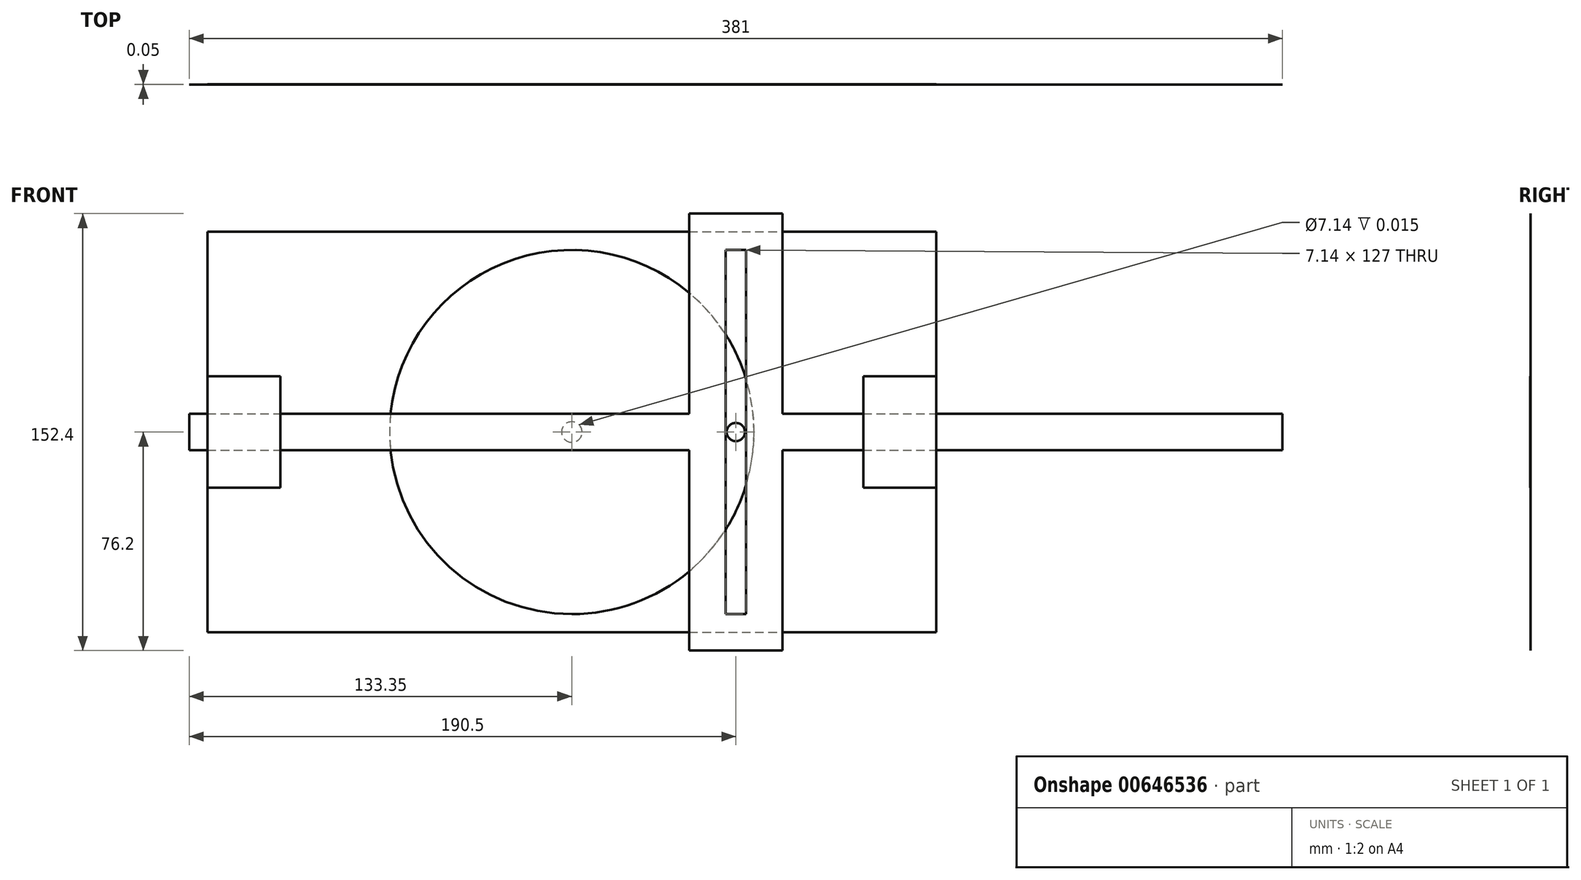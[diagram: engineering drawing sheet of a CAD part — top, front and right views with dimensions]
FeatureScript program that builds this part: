
annotation { "Feature Type Name" : "Feature", "Feature Type Description" : "" }
export const myFeature = defineFeature(function(context is Context, id is Id, definition is map)
    precondition{}
    {
        {
            assignVariable(context, id + "F0", {"name" : "tol", "anyValue" : 1 / 1625.6 * mm});
        }
        {
            assignVariable(context, id + "F1", {"name" : "mat", "anyValue" : 3 / 203.2 * mm});
        }
        {
            var Q0;
            Q0=qCreatedBy(makeId("Front.planeOp"),FACE);
            var sketch = newSketch(context, id + "F2", { "sketchPlane" : qUnion([Q0])});
            skCircle(sketch, "E0", {"center": v(0, 0) * mm, "radius": 63.5 * mm});
            skCircle(sketch, "E1", {"center": v(0, 0) * mm, "radius": 3.18 * mm});
            skCircle(sketch, "E2.0", {"center": v(0, 0) * mm, "radius": 3.57 * mm});
            skSolve(sketch);
        }
        {
            var Q0;
            Q0=makeQuery(id+"F2.imprint","IMPRINT",FACE,{"disambiguationData":[TD([[makeQuery(id+"F2.imprint","IMPRINT",EDGE,{"derivedFrom":sQuery(id+"F2.wireOp",EDGE,"E0")}),1.0]])]});
            extrude(context, id + "F3", {"entities" : qUnion([Q0]), "depth" : getVariable(context, 'mat'), "offsetDistance" : 25.4 * mm});
        }
        {
            var Q0;
            Q0=makeQuery(id+"F3.opExtrude","CAP_FACE",FACE,{"disambiguationData":[OSD([sQuery(id+"F2.wireOp",EDGE,"E0"),sQuery(id+"F2.wireOp",EDGE,"E2.0")])],"isStart":false});
            var sketch = newSketch(context, id + "F4", { "sketchPlane" : qUnion([Q0])});
            skCircle(sketch, "E3", {"center": v(57.15, 0) * mm, "radius": 3.18 * mm});
            skSolve(sketch);
        }
        {
            var Q0;
            Q0=makeQuery(id+"F4.imprint","IMPRINT",FACE,{"disambiguationData":[TD([[makeQuery(id+"F4.imprint","IMPRINT",EDGE,{"derivedFrom":sQuery(id+"F4.wireOp",EDGE,"E3")}),1.0]])]});
            extrude(context, id + "F5", {"entities" : qUnion([Q0]), "operationType" : NewBodyOperationType.ADD, "depth" : getVariable(context, 'mat') * 2, "offsetDistance" : 25.4 * mm});
        }
        {
            var Q0;
            Q0=makeQuery(id+"F3.opExtrude","CAP_FACE",FACE,{"disambiguationData":[OSD([sQuery(id+"F2.wireOp",EDGE,"E0"),sQuery(id+"F2.wireOp",EDGE,"E2.0")])],"isStart":false});
            var sketch = newSketch(context, id + "F6", { "sketchPlane" : qUnion([Q0])});
            skLineSegment(sketch, "E4.bottom", {"start": v(60.72, 63.5) * mm, "end": v(53.58, 63.5) * mm});
            skLineSegment(sketch, "E4.top", {"start": v(60.72, -63.5) * mm, "end": v(53.58, -63.5) * mm});
            skLineSegment(sketch, "E4.left", {"start": v(60.72, 63.5) * mm, "end": v(60.72, -63.5) * mm});
            skLineSegment(sketch, "E4.right", {"start": v(53.58, 63.5) * mm, "end": v(53.58, -63.5) * mm});
            skPoint(sketch, "E4.middle", {"position": v(57.15, 0) * mm});
            skLineSegment(sketch, "E5.bottom", {"start": v(40.88, 76.2) * mm, "end": v(73.42, 76.2) * mm});
            skLineSegment(sketch, "E5.top", {"start": v(40.88, -76.2) * mm, "end": v(73.42, -76.2) * mm});
            skLineSegment(sketch, "E5.left", {"start": v(40.88, 76.2) * mm, "end": v(40.88, -76.2) * mm});
            skLineSegment(sketch, "E5.right", {"start": v(73.42, 76.2) * mm, "end": v(73.42, -76.2) * mm});
            skLineSegment(sketch, "E6.bottom", {"start": v(-133.35, 6.35) * mm, "end": v(247.65, 6.35) * mm});
            skLineSegment(sketch, "E6.top", {"start": v(-133.35, -6.35) * mm, "end": v(247.65, -6.35) * mm});
            skLineSegment(sketch, "E6.left", {"start": v(-133.35, 6.35) * mm, "end": v(-133.35, -6.35) * mm});
            skLineSegment(sketch, "E6.right", {"start": v(247.65, 6.35) * mm, "end": v(247.65, -6.35) * mm});
            skSolve(sketch);
        }
        {
            var Q0;
            Q0 = qSketchRegion(id + "F6", true);
            extrude(context, id + "F7", {"entities" : qUnion([Q0]), "depth" : getVariable(context, 'mat'), "offsetDistance" : 25.4 * mm});
        }
        {
            var Q0;
            Q0=qCreatedBy(makeId("Front.planeOp"),FACE);
            var sketch = newSketch(context, id + "F8", { "sketchPlane" : qUnion([Q0])});
            skLineSegment(sketch, "E7.bottom", {"start": v(-127, 69.85) * mm, "end": v(127, 69.85) * mm});
            skLineSegment(sketch, "E7.top", {"start": v(-127, -69.85) * mm, "end": v(127, -69.85) * mm});
            skLineSegment(sketch, "E7.left", {"start": v(-127, 69.85) * mm, "end": v(-127, -69.85) * mm});
            skLineSegment(sketch, "E7.right", {"start": v(127, 69.85) * mm, "end": v(127, -69.85) * mm});
            skPoint(sketch, "E7.middle", {"position": v(0, 0) * mm});
            skSolve(sketch);
        }
        {
            var Q0;
            Q0=makeQuery(id+"F8.imprint","IMPRINT",FACE,{"disambiguationData":[TD([[makeQuery(id+"F8.imprint","IMPRINT",EDGE,{"derivedFrom":sQuery(id+"F8.wireOp",EDGE,"E7.bottom")}),-1.0]])]});
            extrude(context, id + "F9", {"entities" : qUnion([Q0]), "operationType" : NewBodyOperationType.ADD, "oppositeDirection" : true, "depth" : getVariable(context, 'mat'), "offsetDistance" : 25.4 * mm});
        }
        {
            var Q0;
            {var subQ0=sQuery(id+"F8.wireOp",EDGE,"E7.left");var subQ1=sQuery(id+"F8.wireOp",EDGE,"E7.top");var subQ2=sQuery(id+"F8.wireOp",EDGE,"E7.bottom");var subQ3=sQuery(id+"F8.wireOp",EDGE,"E7.right");Q0=makeQuery(id+"F9.boolean.opBoolean","SPLIT",FACE,{"disambiguationData":[TD([makeQuery(id+"F3.opExtrude","SWEPT_FACE",FACE,{"disambiguationData":[OSD([sQuery(id+"F2.wireOp",EDGE,"E0")])]})])],"derivedFrom":makeQuery(id+"F9.opExtrude","CAP_FACE",FACE,{"disambiguationData":[OSD([subQ2,subQ1,subQ0,subQ3])],"isStart":true})});}
            var sketch = newSketch(context, id + "F10", { "sketchPlane" : qUnion([Q0])});
            skPoint(sketch, "E8.middle", {"position": v(-127, 0) * mm});
            skLineSegment(sketch, "E9", {"start": v(-127, 0) * mm, "end": v(-127, 19.45) * mm});
            skLineSegment(sketch, "E10", {"start": v(-127, 19.45) * mm, "end": v(-101.6, 19.45) * mm});
            skLineSegment(sketch, "E11", {"start": v(-127, 0) * mm, "end": v(-127, -19.45) * mm});
            skLineSegment(sketch, "E12", {"start": v(-127, -19.45) * mm, "end": v(-101.6, -19.45) * mm});
            skLineSegment(sketch, "E13", {"start": v(-101.6, 19.45) * mm, "end": v(-101.6, -19.45) * mm});
            skLineSegment(sketch, "E14", {"start": v(127, 0) * mm, "end": v(127, 19.45) * mm});
            skLineSegment(sketch, "E15", {"start": v(127, 0) * mm, "end": v(127, -19.45) * mm});
            skLineSegment(sketch, "E16", {"start": v(127, 19.45) * mm, "end": v(101.6, 19.45) * mm});
            skLineSegment(sketch, "E17", {"start": v(127, -19.45) * mm, "end": v(101.6, -19.45) * mm});
            skLineSegment(sketch, "E18", {"start": v(101.6, -19.45) * mm, "end": v(101.6, 19.45) * mm});
            skSolve(sketch);
        }
        {
            var Q0;
            Q0=makeQuery(id+"F10.imprint","IMPRINT",FACE,{"disambiguationData":[TD([[makeQuery(id+"F10.imprint","IMPRINT",EDGE,{"derivedFrom":sQuery(id+"F10.wireOp",EDGE,"E9")}),1.0]])]});
            var Q1;
            Q1=makeQuery(id+"F10.imprint","IMPRINT",FACE,{"disambiguationData":[TD([[makeQuery(id+"F10.imprint","IMPRINT",EDGE,{"derivedFrom":sQuery(id+"F10.wireOp",EDGE,"E14")}),-1.0]])]});
            extrude(context, id + "F11", {"entities" : qUnion([Q0, Q1]), "depth" : getVariable(context, 'mat') * 3 + getVariable(context, 'tol'), "offsetDistance" : 25.4 * mm});
        }
    });
